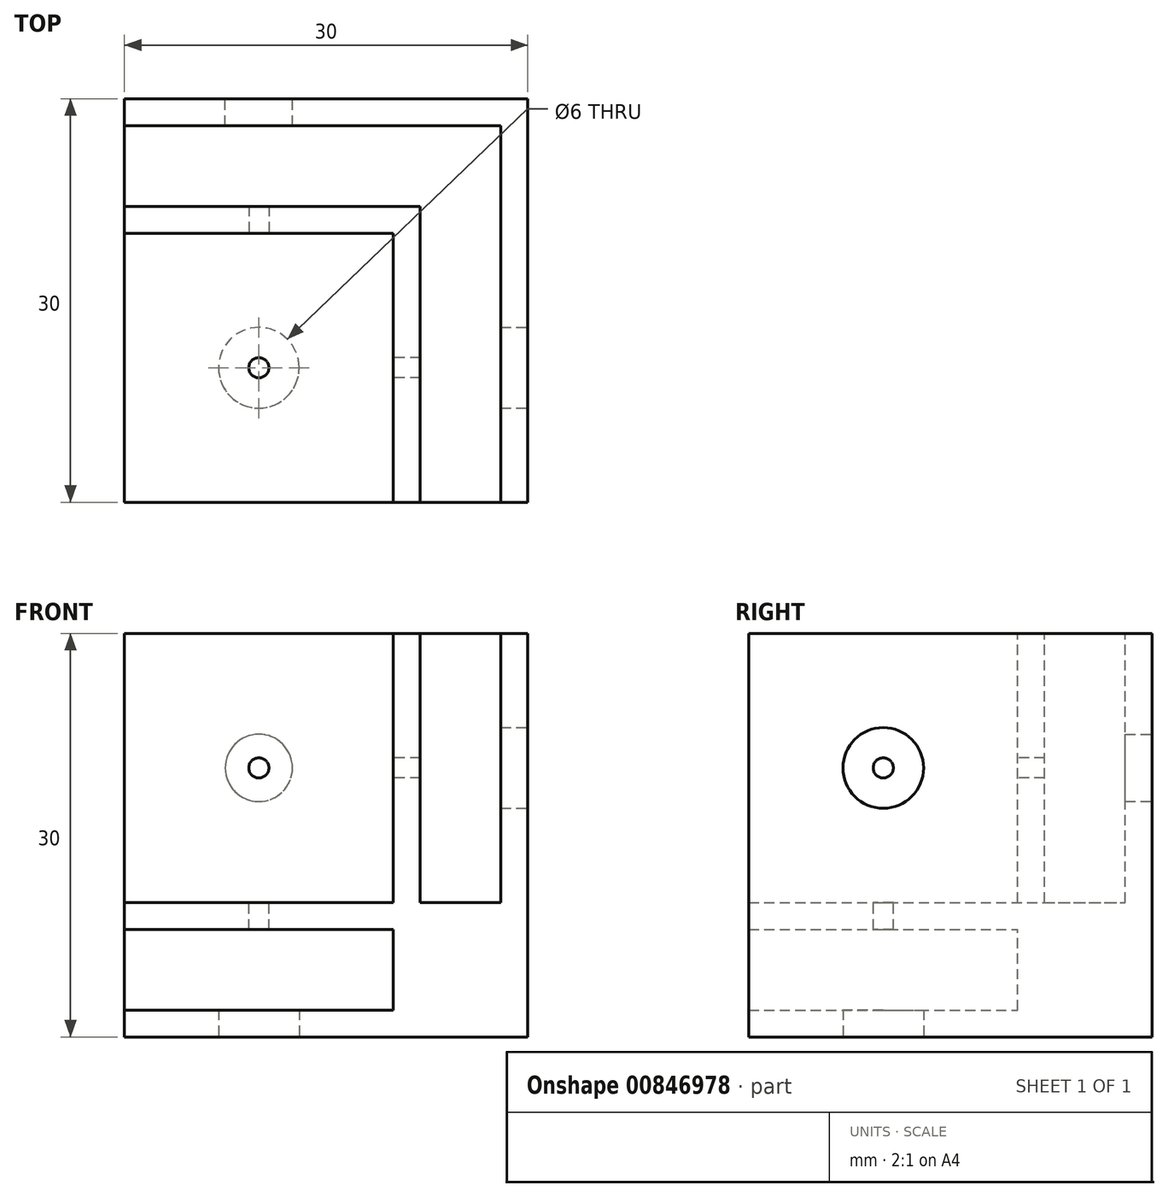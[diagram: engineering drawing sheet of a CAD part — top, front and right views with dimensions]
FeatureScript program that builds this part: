
annotation { "Feature Type Name" : "Feature", "Feature Type Description" : "" }
export const myFeature = defineFeature(function(context is Context, id is Id, definition is map)
    precondition{}
    {
        {
            var Q0;
            Q0=qCreatedBy(makeId("Top.planeOp"),FACE);
            var sketch = newSketch(context, id + "F0", { "sketchPlane" : qUnion([Q0])});
            skLineSegment(sketch, "E0.bottom", {"start": v(0, 0) * mm, "end": v(30, 0) * mm});
            skLineSegment(sketch, "E0.top", {"start": v(0, 30) * mm, "end": v(30, 30) * mm});
            skLineSegment(sketch, "E0.left", {"start": v(0, 0) * mm, "end": v(0, 30) * mm});
            skLineSegment(sketch, "E0.right", {"start": v(30, 0) * mm, "end": v(30, 30) * mm});
            skSolve(sketch);
        }
        {
            var Q0;
            Q0 = qSketchRegion(id + "F0", true);
            extrude(context, id + "F1", {"entities" : qUnion([Q0]), "depth" : 30 * mm, "offsetDistance" : 25 * mm});
        }
        {
            var Q0;
            Q0=makeQuery(id+"F1.opExtrude","CAP_FACE",FACE,{"disambiguationData":[OSD([sQuery(id+"F0.wireOp",EDGE,"E0.bottom"),sQuery(id+"F0.wireOp",EDGE,"E0.top"),sQuery(id+"F0.wireOp",EDGE,"E0.left"),sQuery(id+"F0.wireOp",EDGE,"E0.right")])],"isStart":false});
            var sketch = newSketch(context, id + "F2", { "sketchPlane" : qUnion([Q0])});
            skLineSegment(sketch, "E1.bottom", {"start": v(0, 0) * mm, "end": v(20, 0) * mm});
            skLineSegment(sketch, "E1.top", {"start": v(0, 20) * mm, "end": v(20, 20) * mm});
            skLineSegment(sketch, "E1.left", {"start": v(0, 0) * mm, "end": v(0, 20) * mm});
            skLineSegment(sketch, "E1.right", {"start": v(20, 0) * mm, "end": v(20, 20) * mm});
            skSolve(sketch);
        }
        {
            var Q0;
            Q0 = qSketchRegion(id + "F2", true);
            extrude(context, id + "F3", {"entities" : qUnion([Q0]), "operationType" : NewBodyOperationType.REMOVE, "oppositeDirection" : true, "depth" : 20 * mm, "offsetDistance" : 25 * mm});
        }
        {
            var Q0;
            Q0=makeQuery(id+"F1.opExtrude","CAP_FACE",FACE,{"disambiguationData":[OSD([sQuery(id+"F0.wireOp",EDGE,"E0.bottom"),sQuery(id+"F0.wireOp",EDGE,"E0.top"),sQuery(id+"F0.wireOp",EDGE,"E0.left"),sQuery(id+"F0.wireOp",EDGE,"E0.right")])],"isStart":false});
            var sketch = newSketch(context, id + "F4", { "sketchPlane" : qUnion([Q0])});
            skLineSegment(sketch, "E2.bottom", {"start": v(0, 28) * mm, "end": v(28, 28) * mm});
            skLineSegment(sketch, "E2.top", {"start": v(0, 22) * mm, "end": v(22, 22) * mm});
            skLineSegment(sketch, "E2.left", {"start": v(0, 28) * mm, "end": v(0, 22) * mm});
            skLineSegment(sketch, "E3.bottom", {"start": v(22, 0) * mm, "end": v(28, 0) * mm});
            skLineSegment(sketch, "E3.left", {"start": v(22, 0) * mm, "end": v(22, 22) * mm});
            skLineSegment(sketch, "E3.right", {"start": v(28, 0) * mm, "end": v(28, 22) * mm});
            skLineSegment(sketch, "E4", {"start": v(28, 22) * mm, "end": v(28, 28) * mm});
            skSolve(sketch);
        }
        {
            var Q0;
            Q0 = qSketchRegion(id + "F4", true);
            extrude(context, id + "F5", {"entities" : qUnion([Q0]), "operationType" : NewBodyOperationType.REMOVE, "oppositeDirection" : true, "depth" : 20 * mm, "offsetDistance" : 25 * mm});
        }
        {
            var Q0;
            Q0=makeQuery(id+"F1.opExtrude","SWEPT_FACE",FACE,{"disambiguationData":[OSD([sQuery(id+"F0.wireOp",EDGE,"E0.left")])]});
            var sketch = newSketch(context, id + "F6", { "sketchPlane" : qUnion([Q0])});
            skLineSegment(sketch, "E5.bottom", {"start": v(0, 2) * mm, "end": v(-20, 2) * mm});
            skLineSegment(sketch, "E5.top", {"start": v(0, 8) * mm, "end": v(-20, 8) * mm});
            skLineSegment(sketch, "E5.left", {"start": v(0, 2) * mm, "end": v(0, 8) * mm});
            skLineSegment(sketch, "E5.right", {"start": v(-20, 2) * mm, "end": v(-20, 8) * mm});
            skSolve(sketch);
        }
        {
            var Q0;
            Q0 = qSketchRegion(id + "F6", true);
            extrude(context, id + "F7", {"entities" : qUnion([Q0]), "operationType" : NewBodyOperationType.REMOVE, "oppositeDirection" : true, "depth" : 20 * mm, "offsetDistance" : 25 * mm});
        }
        {
            var Q0;
            Q0=makeQuery(id+"F1.opExtrude","SWEPT_FACE",FACE,{"disambiguationData":[OSD([sQuery(id+"F0.wireOp",EDGE,"E0.top")])]});
            var sketch = newSketch(context, id + "F8", { "sketchPlane" : qUnion([Q0])});
            skLineSegment(sketch, "E6", {"start": v(-10, 0) * mm, "end": v(-10, 30) * mm, "construction": true});
            skLineSegment(sketch, "E7", {"start": v(0, 20) * mm, "end": v(-30, 20) * mm, "construction": true});
            skCircle(sketch, "E8", {"center": v(-10, 20) * mm, "radius": 2.5 * mm});
            skSolve(sketch);
        }
        {
            var Q0;
            Q0 = qSketchRegion(id + "F8", true);
            extrude(context, id + "F9", {"entities" : qUnion([Q0]), "operationType" : NewBodyOperationType.REMOVE, "endBound" : BoundingType.UP_TO_NEXT, "oppositeDirection" : true, "depth" : 25 * mm, "offsetDistance" : 25 * mm});
        }
        {
            var Q0;
            Q0=makeQuery(id+"F3.boolean.opBoolean","COPY",FACE,{"derivedFrom":makeQuery(id+"F3.opExtrude","SWEPT_FACE",FACE,{"disambiguationData":[OSD([sQuery(id+"F2.wireOp",EDGE,"E1.top")])]})});
            var sketch = newSketch(context, id + "F10", { "sketchPlane" : qUnion([Q0])});
            skLineSegment(sketch, "E9", {"start": v(10, 30) * mm, "end": v(10, 10) * mm, "construction": true});
            skCircle(sketch, "E10", {"center": v(10, 20) * mm, "radius": 0.75 * mm});
            skSolve(sketch);
        }
        {
            var Q0;
            Q0 = qSketchRegion(id + "F10", true);
            extrude(context, id + "F11", {"entities" : qUnion([Q0]), "operationType" : NewBodyOperationType.REMOVE, "oppositeDirection" : true, "depth" : 25 * mm, "offsetDistance" : 25 * mm});
        }
        {
            var Q0;
            Q0=makeQuery(id+"F1.opExtrude","SWEPT_FACE",FACE,{"disambiguationData":[OSD([sQuery(id+"F0.wireOp",EDGE,"E0.right")])]});
            var sketch = newSketch(context, id + "F12", { "sketchPlane" : qUnion([Q0])});
            skLineSegment(sketch, "E11", {"start": v(0, 20) * mm, "end": v(30, 20) * mm, "construction": true});
            skLineSegment(sketch, "E12", {"start": v(10, 30) * mm, "end": v(10, 0) * mm, "construction": true});
            skCircle(sketch, "E13", {"center": v(10, 20) * mm, "radius": 3 * mm});
            skSolve(sketch);
        }
        {
            var Q0;
            Q0 = qSketchRegion(id + "F12", true);
            extrude(context, id + "F13", {"entities" : qUnion([Q0]), "operationType" : NewBodyOperationType.REMOVE, "endBound" : BoundingType.UP_TO_NEXT, "oppositeDirection" : true, "depth" : 25 * mm, "offsetDistance" : 25 * mm});
        }
        {
            var Q0;
            Q0=makeQuery(id+"F3.boolean.opBoolean","COPY",FACE,{"derivedFrom":makeQuery(id+"F3.opExtrude","SWEPT_FACE",FACE,{"disambiguationData":[OSD([sQuery(id+"F2.wireOp",EDGE,"E1.right")])]})});
            var sketch = newSketch(context, id + "F14", { "sketchPlane" : qUnion([Q0])});
            skLineSegment(sketch, "E14", {"start": v(-10, 10) * mm, "end": v(-10, 30) * mm, "construction": true});
            skLineSegment(sketch, "E15", {"start": v(0, 20) * mm, "end": v(-20, 20) * mm, "construction": true});
            skCircle(sketch, "E16", {"center": v(-10, 20) * mm, "radius": 0.75 * mm});
            skSolve(sketch);
        }
        {
            var Q0;
            Q0 = qSketchRegion(id + "F14", true);
            extrude(context, id + "F15", {"entities" : qUnion([Q0]), "operationType" : NewBodyOperationType.REMOVE, "endBound" : BoundingType.UP_TO_NEXT, "oppositeDirection" : true, "depth" : 25 * mm, "offsetDistance" : 25 * mm});
        }
        {
            var Q0;
            Q0=makeQuery(id+"F3.boolean.opBoolean","COPY",FACE,{"derivedFrom":makeQuery(id+"F3.opExtrude","CAP_FACE",FACE,{"disambiguationData":[OSD([sQuery(id+"F2.wireOp",EDGE,"E1.bottom"),sQuery(id+"F2.wireOp",EDGE,"E1.top"),sQuery(id+"F2.wireOp",EDGE,"E1.left"),sQuery(id+"F2.wireOp",EDGE,"E1.right")])],"isStart":false})});
            var sketch = newSketch(context, id + "F16", { "sketchPlane" : qUnion([Q0])});
            skLineSegment(sketch, "E17", {"start": v(10, 0) * mm, "end": v(10, 20) * mm, "construction": true});
            skCircle(sketch, "E18", {"center": v(10, 10) * mm, "radius": 0.75 * mm});
            skSolve(sketch);
        }
        {
            var Q0;
            Q0 = qSketchRegion(id + "F16", true);
            extrude(context, id + "F17", {"entities" : qUnion([Q0]), "operationType" : NewBodyOperationType.REMOVE, "endBound" : BoundingType.UP_TO_NEXT, "oppositeDirection" : true, "depth" : 25 * mm, "offsetDistance" : 25 * mm});
        }
        {
            var Q0;
            Q0=makeQuery(id+"F1.opExtrude","CAP_FACE",FACE,{"disambiguationData":[OSD([sQuery(id+"F0.wireOp",EDGE,"E0.bottom"),sQuery(id+"F0.wireOp",EDGE,"E0.top"),sQuery(id+"F0.wireOp",EDGE,"E0.left"),sQuery(id+"F0.wireOp",EDGE,"E0.right")])],"isStart":true});
            var sketch = newSketch(context, id + "F18", { "sketchPlane" : qUnion([Q0])});
            skLineSegment(sketch, "E19", {"start": v(10, 0) * mm, "end": v(10, -30) * mm, "construction": true});
            skLineSegment(sketch, "E20", {"start": v(0, -10) * mm, "end": v(30, -10) * mm, "construction": true});
            skCircle(sketch, "E21", {"center": v(10, -10) * mm, "radius": 3 * mm});
            skSolve(sketch);
        }
        {
            var Q0;
            Q0 = qSketchRegion(id + "F18", true);
            extrude(context, id + "F19", {"entities" : qUnion([Q0]), "operationType" : NewBodyOperationType.REMOVE, "endBound" : BoundingType.UP_TO_NEXT, "oppositeDirection" : true, "depth" : 25 * mm, "offsetDistance" : 25 * mm});
        }
    });
